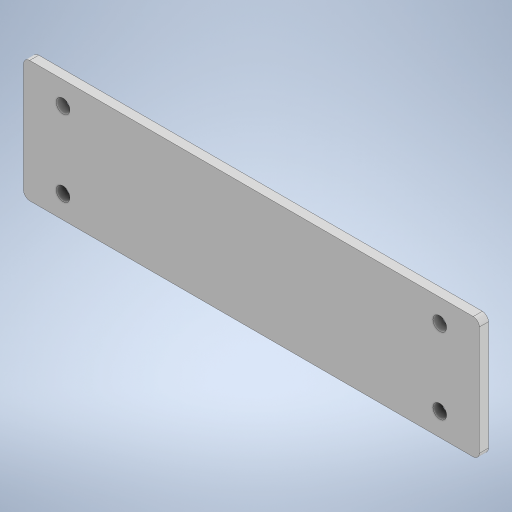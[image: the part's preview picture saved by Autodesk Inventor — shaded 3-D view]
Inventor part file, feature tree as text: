
AUTODESK INVENTOR PART (.ipt)
format: ipt  version: 2024 (Build 280153000, 153)  size: 230,400 bytes
history: native  units: mm
features: extrude x2, sketch x2, fillet x1
ambient origin geometry x8: Origin, YZ Plane, XZ Plane, XY Plane, X Axis, Y Axis, Z Axis, Center Point
bodies: Volumenkörper1 (feature_tree)
feature tree (5):
  extrude  "Extrusion1"  Depth=150.0mm
  extrude  "Extrusion2"  Depth=2.0mm
  fillet  "Rundung1"  Radius=4.5mm
  sketch  "Skizze1"  dims[d0=40.0mm d1=150.0mm]
  sketch  "Skizze2"  dims[d2=3.0mm d3=0.0mm d4=13.0mm d5=4.5mm d6=4.5mm d7=25.0mm d8=3.0mm d9=0.0mm d10=2.0mm]
